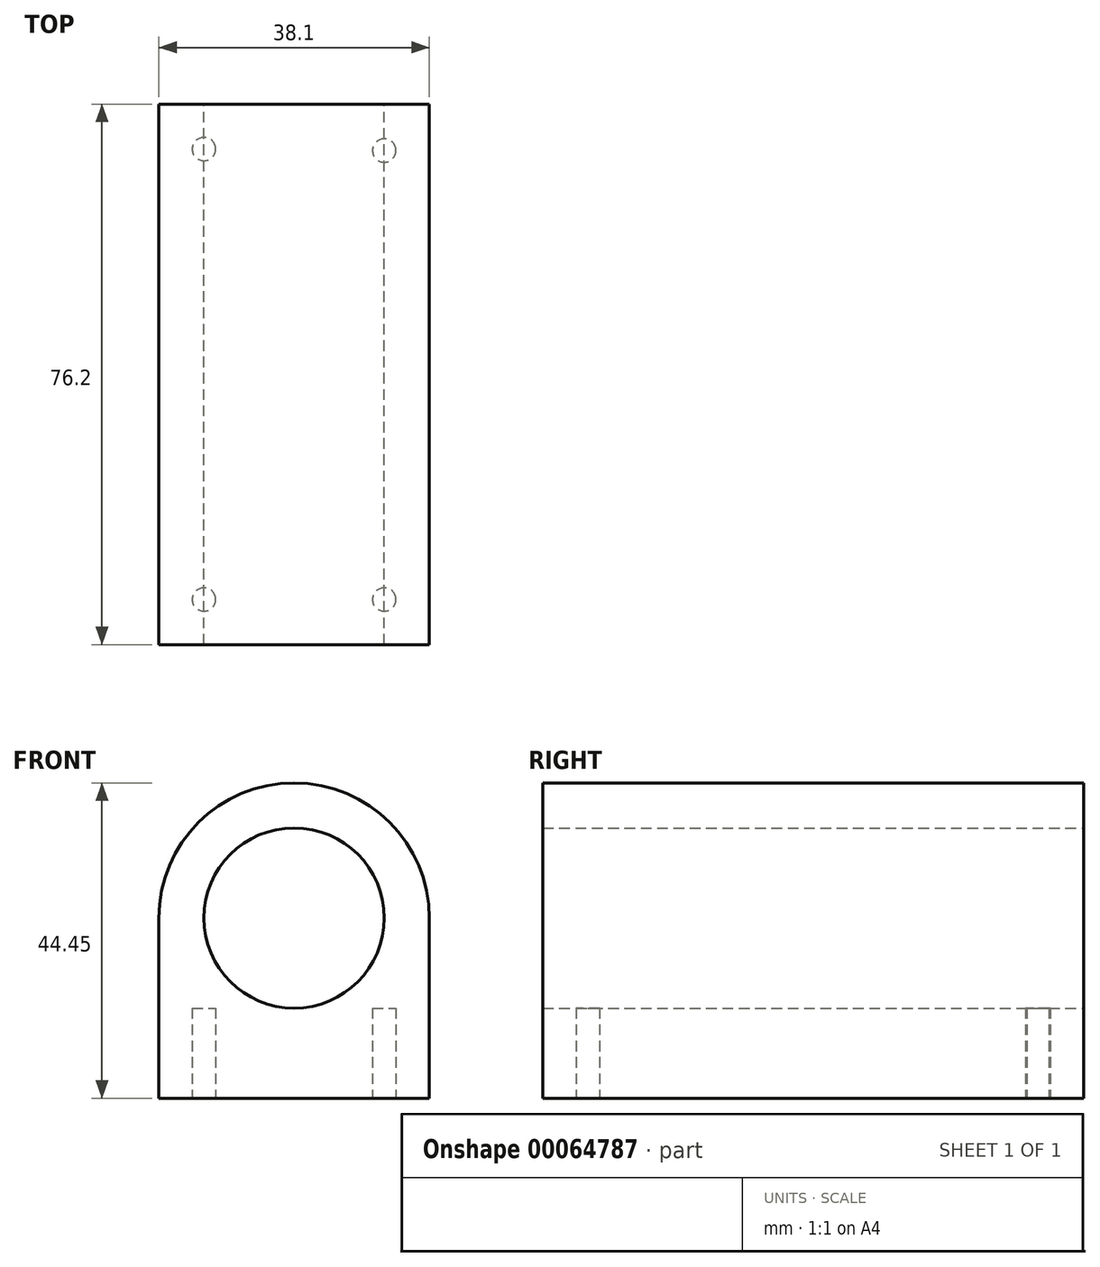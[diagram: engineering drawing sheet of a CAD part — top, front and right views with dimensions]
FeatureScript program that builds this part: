
annotation { "Feature Type Name" : "Feature", "Feature Type Description" : "" }
export const myFeature = defineFeature(function(context is Context, id is Id, definition is map)
    precondition{}
    {
        {
            var Q0;
            Q0=qCreatedBy(makeId("Front.planeOp"),FACE);
            var sketch = newSketch(context, id + "F0", { "sketchPlane" : qUnion([Q0])});
            skCircle(sketch, "E0", {"center": v(0, 0) * mm, "radius": 12.7 * mm});
            skArc(sketch, "E1", {"start": v(19.05, 0) * mm, "mid": v(0, 19.05) * mm, "end": v(-19.05, 0) * mm});
            skLineSegment(sketch, "E2", {"start": v(-19.05, 0) * mm, "end": v(-19.05, -25.4) * mm});
            skLineSegment(sketch, "E3", {"start": v(-19.05, -25.4) * mm, "end": v(19.05, -25.4) * mm});
            skLineSegment(sketch, "E4", {"start": v(19.05, -25.4) * mm, "end": v(19.05, 0) * mm});
            skSolve(sketch);
        }
        {
            var Q0;
            Q0=makeQuery(id+"F0.imprint","IMPRINT",FACE,{"disambiguationData":[TD([[makeQuery(id+"F0.imprint","IMPRINT",EDGE,{"derivedFrom":sQuery(id+"F0.wireOp",EDGE,"E0")}),-1.0]])]});
            extrude(context, id + "F1", {"entities" : qUnion([Q0]), "depth" : 76.2 * mm});
        }
        {
            var Q0;
            Q0=makeQuery(id+"F1.opExtrude","SWEPT_FACE",FACE,{"disambiguationData":[OSD([sQuery(id+"F0.wireOp",EDGE,"E3")])]});
            var sketch = newSketch(context, id + "F2", { "sketchPlane" : qUnion([Q0])});
            skCircle(sketch, "E5", {"center": v(-12.7, 69.85) * mm, "radius": 1.65 * mm});
            skCircle(sketch, "E6", {"center": v(12.7, 69.85) * mm, "radius": 1.65 * mm});
            skCircle(sketch, "E7", {"center": v(-12.7, 6.35) * mm, "radius": 1.65 * mm});
            skCircle(sketch, "E8", {"center": v(12.7, 6.55) * mm, "radius": 1.65 * mm});
            skSolve(sketch);
        }
        {
            var Q0;
            Q0=qSketchRegion(id+"F2",true);
            extrude(context, id + "F3", {"entities" : qUnion([Q0]), "operationType" : NewBodyOperationType.REMOVE, "oppositeDirection" : true, "depth" : 12.7 * mm});
        }
    });
